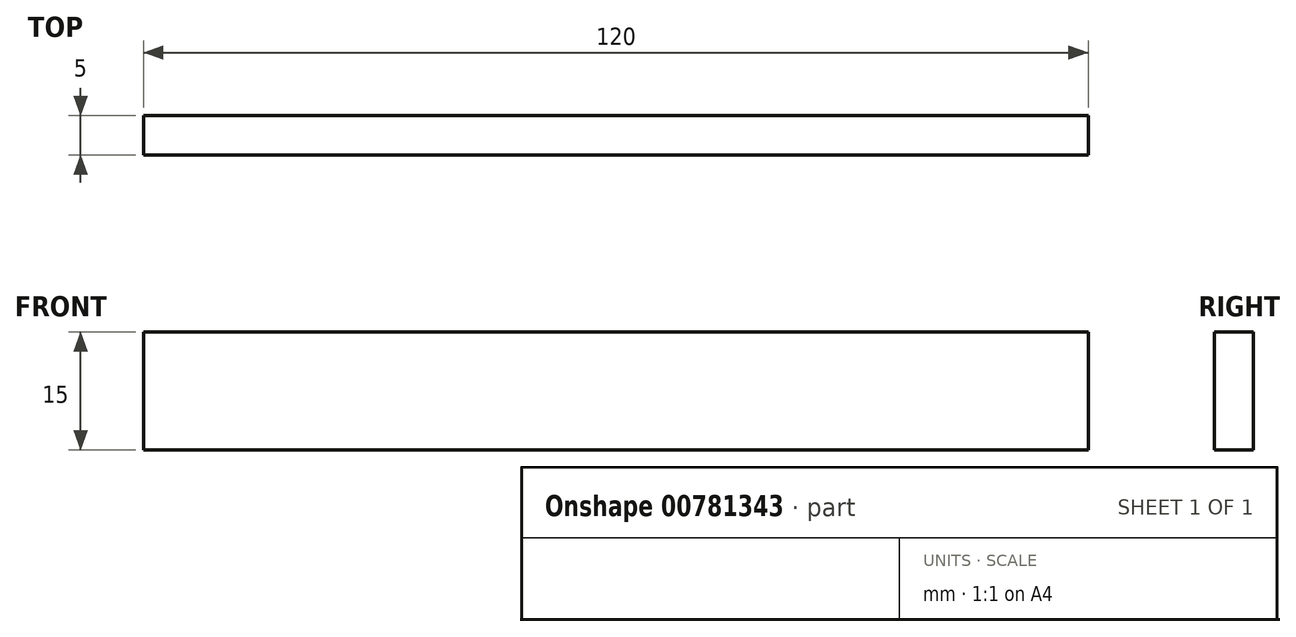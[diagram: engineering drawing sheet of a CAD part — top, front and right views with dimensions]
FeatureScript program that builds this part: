
annotation { "Feature Type Name" : "Feature", "Feature Type Description" : "" }
export const myFeature = defineFeature(function(context is Context, id is Id, definition is map)
    precondition{}
    {
        {
            var Q0;
            Q0=qCreatedBy(makeId("Front.planeOp"),FACE);
            var sketch = newSketch(context, id + "F0", { "sketchPlane" : qUnion([Q0])});
            skLineSegment(sketch, "E0.bottom", {"start": v(60, 7.5) * mm, "end": v(-60, 7.5) * mm});
            skLineSegment(sketch, "E0.top", {"start": v(60, -7.5) * mm, "end": v(-60, -7.5) * mm});
            skLineSegment(sketch, "E0.left", {"start": v(60, 7.5) * mm, "end": v(60, -7.5) * mm});
            skLineSegment(sketch, "E0.right", {"start": v(-60, 7.5) * mm, "end": v(-60, -7.5) * mm});
            skPoint(sketch, "E0.middle", {"position": v(0, 0) * mm});
            skSolve(sketch);
        }
        {
            var Q0;
            Q0 = qSketchRegion(id + "F0", true);
            extrude(context, id + "F1", {"entities" : qUnion([Q0]), "depth" : 5 * mm, "offsetDistance" : 25 * mm});
        }
    });
